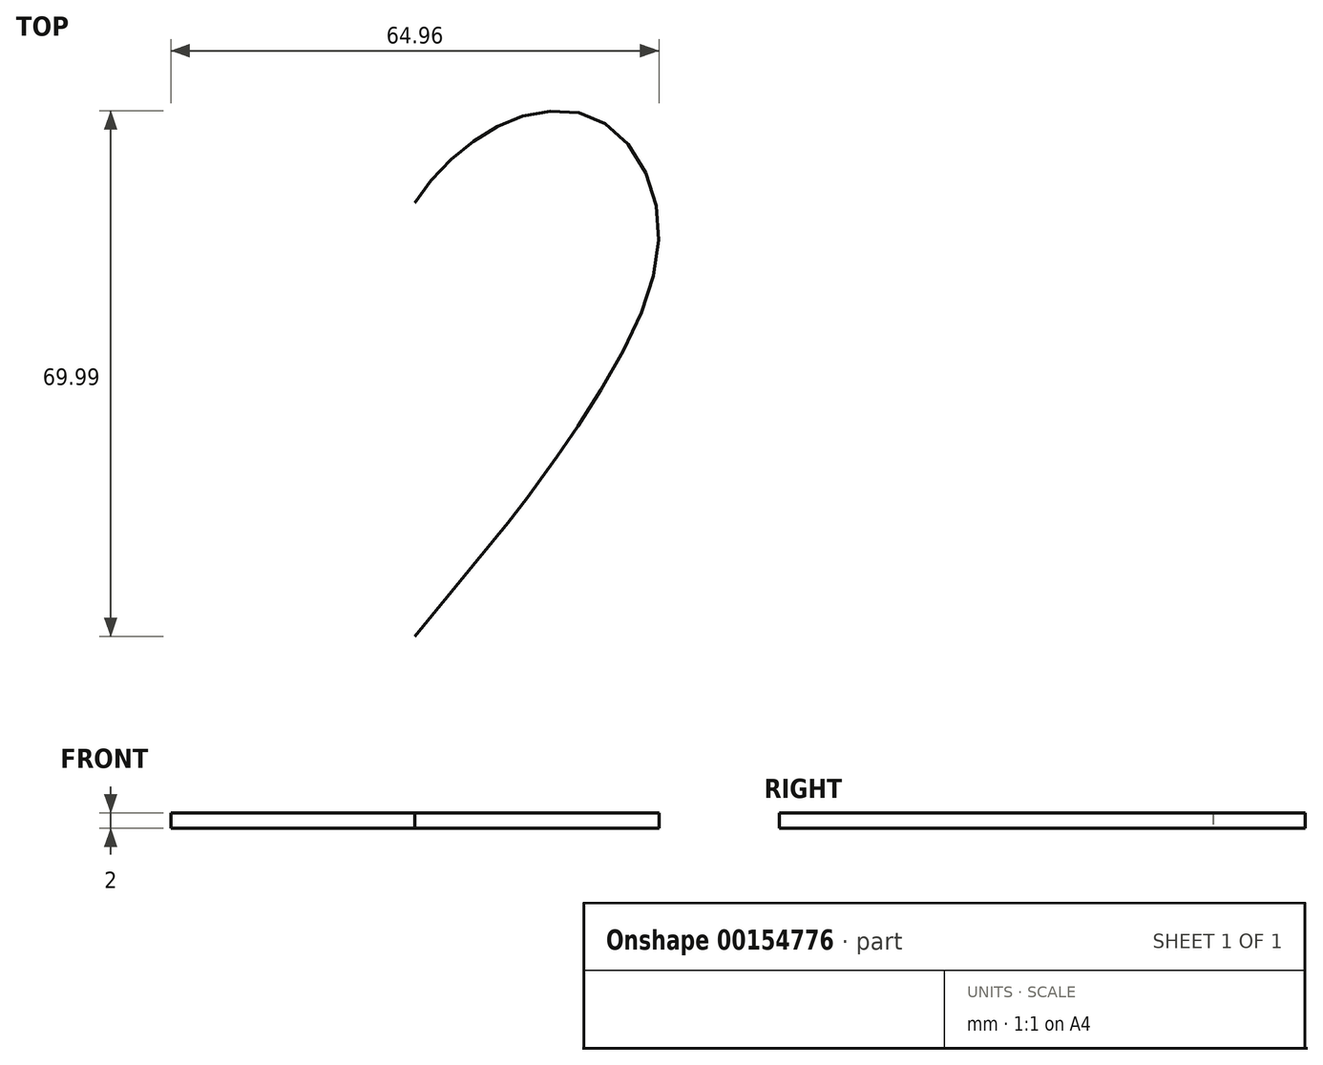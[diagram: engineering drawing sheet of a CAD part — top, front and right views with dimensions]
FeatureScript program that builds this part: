
annotation { "Feature Type Name" : "Feature", "Feature Type Description" : "" }
export const myFeature = defineFeature(function(context is Context, id is Id, definition is map)
    precondition{}
    {
        {
            var Q0;
            Q0=qCreatedBy(makeId("Top.planeOp"),FACE);
            var sketch = newSketch(context, id + "F0", { "sketchPlane" : qUnion([Q0])});
            skLineSegment(sketch, "E0", {"start": v(0, 21.6) * mm, "end": v(0, -36.15) * mm});
            skFitSpline(sketch, "E1", {"points": [v(0, 21.6) * mm, v(6.87, 29.12) * mm, v(15.63, 33.45) * mm, v(25.38, 32.13) * mm, v(32.2, 20.81) * mm, v(28.78, 3.91) * mm, v(17.8, -13.77) * mm, v(0, -36.15) * mm], "startDerivative": vector(43.51, 70.34) * mm, "endDerivative": vector(-223, -272.38) * mm});
            skFitSpline(sketch, "E2.MirrorCS", {"points": [v(0, 21.6) * mm, v(-6.87, 29.12) * mm, v(-15.63, 33.45) * mm, v(-25.38, 32.13) * mm, v(-32.2, 20.81) * mm, v(-28.78, 3.91) * mm, v(-17.8, -13.77) * mm, v(0, -36.15) * mm], "startDerivative": vector(-43.51, 70.34) * mm, "endDerivative": vector(223, -272.38) * mm});
            skCircle(sketch, "E3", {"center": v(0, 0) * mm, "radius": 22.5 * mm, "construction": true});
            skSolve(sketch);
        }
        {
            var Q0;
            Q0=makeQuery(id+"F0.imprint","IMPRINT",FACE,{"disambiguationData":[TD([[makeQuery(id+"F0.imprint","IMPRINT",EDGE,{"derivedFrom":sQuery(id+"F0.wireOp",EDGE,"E0")}),1.0]])]});
            var Q1;
            Q1=makeQuery(id+"F0.imprint","IMPRINT",FACE,{"disambiguationData":[TD([[makeQuery(id+"F0.imprint","IMPRINT",EDGE,{"derivedFrom":sQuery(id+"F0.wireOp",EDGE,"E0")}),-1.0]])]});
            extrude(context, id + "F1", {"entities" : qUnion([Q0, Q1]), "depth" : 2 * mm});
        }
    });
